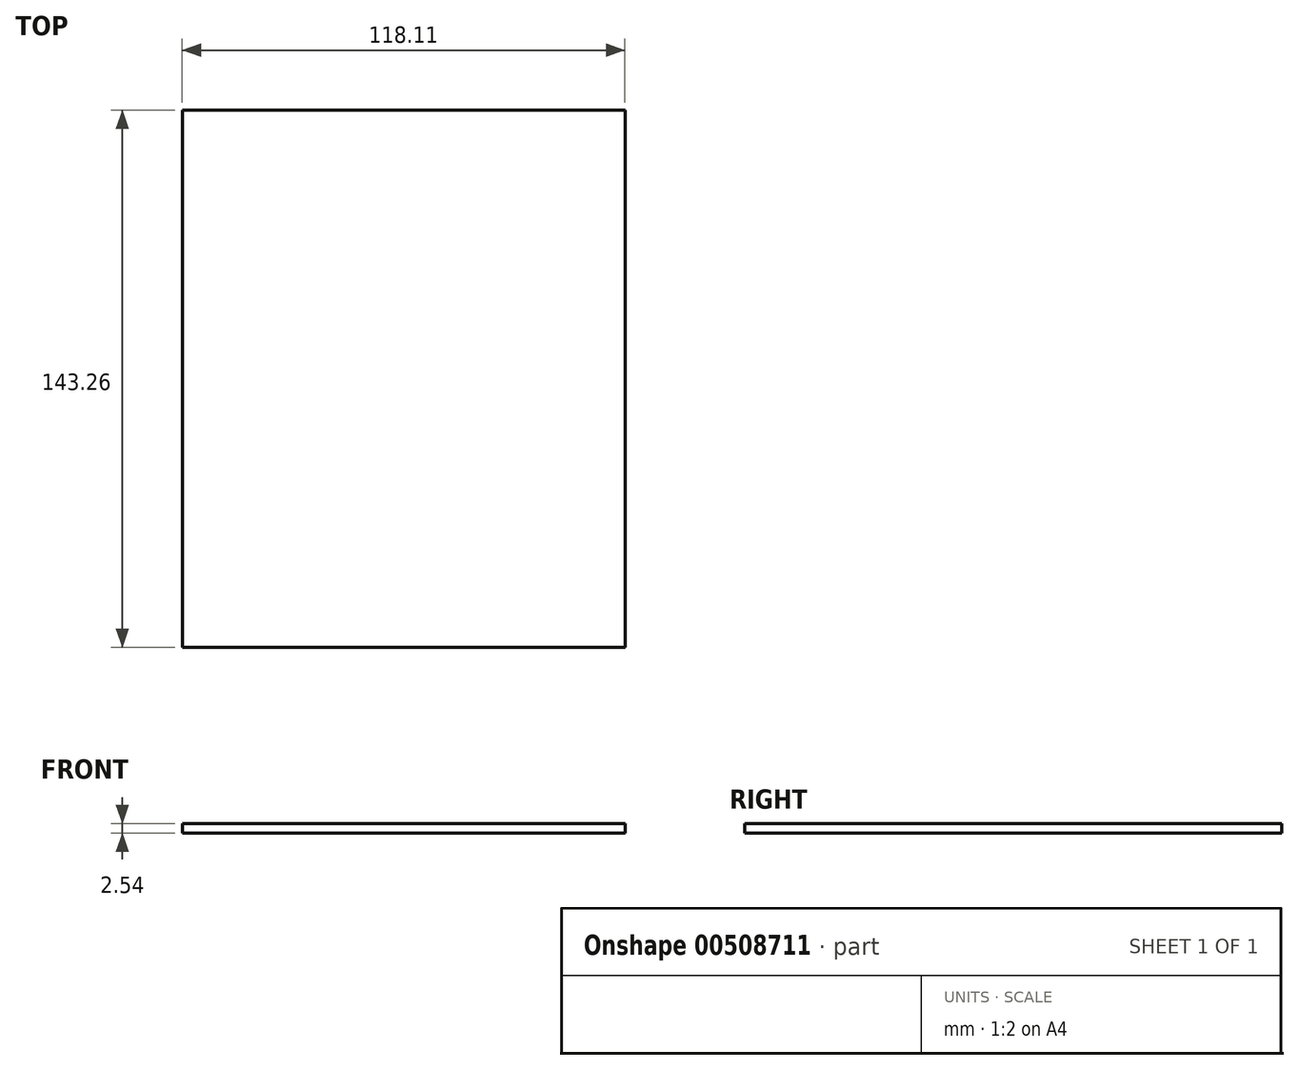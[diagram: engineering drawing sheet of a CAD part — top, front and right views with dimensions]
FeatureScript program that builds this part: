
annotation { "Feature Type Name" : "Feature", "Feature Type Description" : "" }
export const myFeature = defineFeature(function(context is Context, id is Id, definition is map)
    precondition{}
    {
        {
            var Q0;
            Q0=qCreatedBy(makeId("Top.planeOp"),FACE);
            var sketch = newSketch(context, id + "F0", { "sketchPlane" : qUnion([Q0])});
            skLineSegment(sketch, "E0", {"start": v(-48.18, 67.1) * mm, "end": v(-48.18, -76.15) * mm});
            skLineSegment(sketch, "E1", {"start": v(-48.18, -76.15) * mm, "end": v(69.93, -76.15) * mm});
            skLineSegment(sketch, "E2", {"start": v(69.93, -76.15) * mm, "end": v(69.93, 67.1) * mm});
            skLineSegment(sketch, "E3", {"start": v(69.93, 67.1) * mm, "end": v(-48.18, 67.1) * mm});
            skSolve(sketch);
        }
        {
            var Q0;
            Q0=makeQuery(id+"F0.imprint","IMPRINT",FACE,{"disambiguationData":[TD([[makeQuery(id+"F0.imprint","IMPRINT",EDGE,{"derivedFrom":sQuery(id+"F0.wireOp",EDGE,"E0")}),1.0]])]});
            extrude(context, id + "F1", {"entities" : qUnion([Q0]), "depth" : 2.54 * mm, "offsetDistance" : 25.4 * mm});
        }
    });
